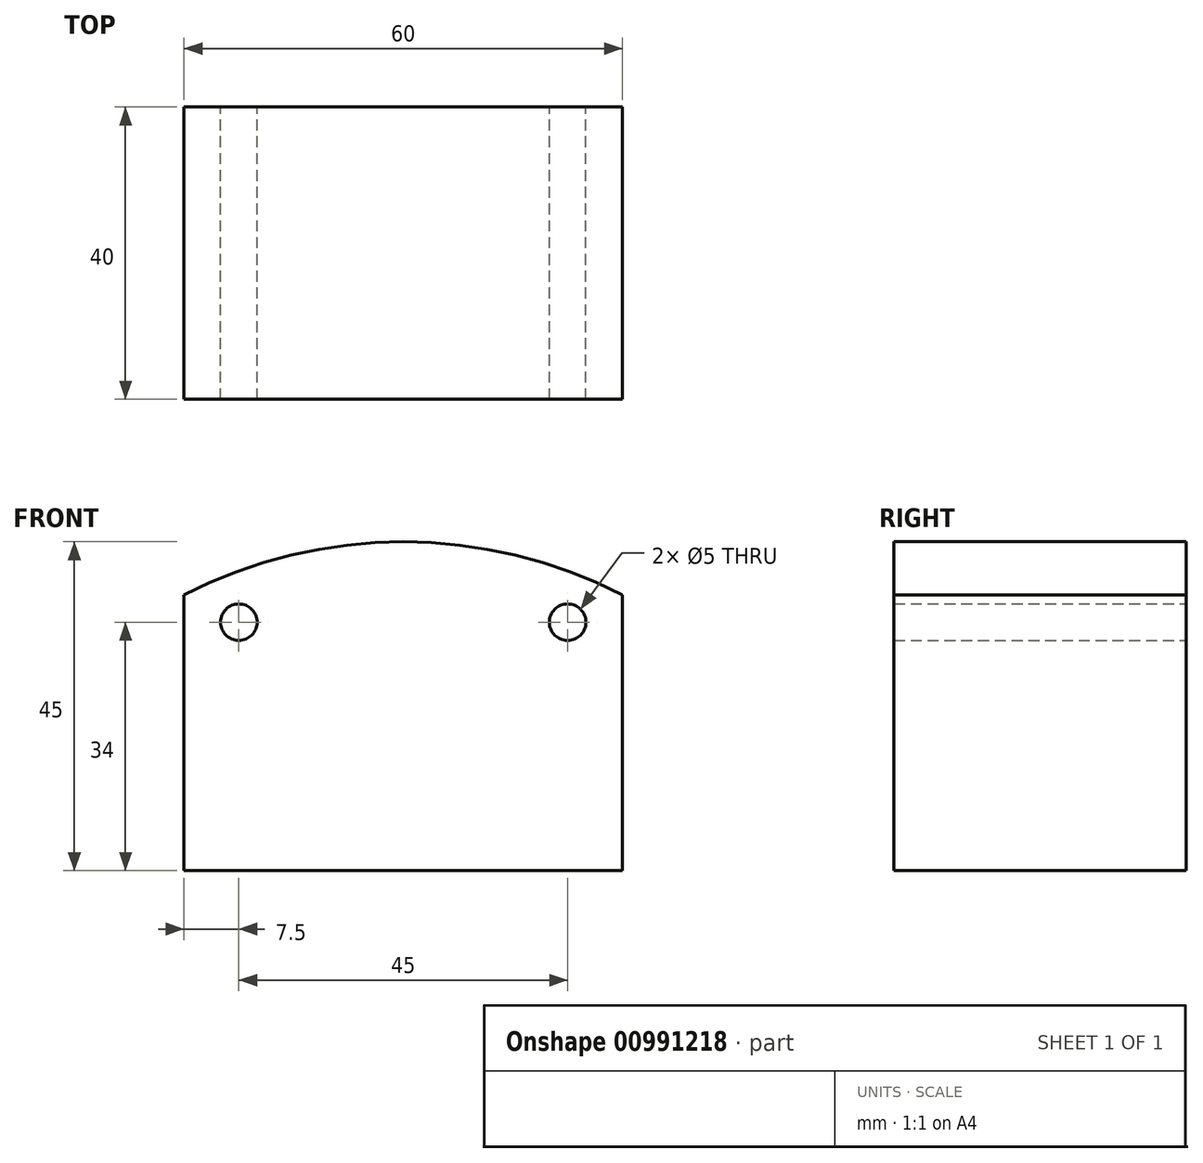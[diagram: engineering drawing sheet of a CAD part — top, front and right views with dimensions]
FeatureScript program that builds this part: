
annotation { "Feature Type Name" : "Feature", "Feature Type Description" : "" }
export const myFeature = defineFeature(function(context is Context, id is Id, definition is map)
    precondition{}
    {
        {
            var Q0;
            Q0=qCreatedBy(makeId("Front.planeOp"),FACE);
            var sketch = newSketch(context, id + "F0", { "sketchPlane" : qUnion([Q0])});
            skLineSegment(sketch, "E0.bottom", {"start": v(0, 0) * mm, "end": v(60, 0) * mm});
            skLineSegment(sketch, "E0.left", {"start": v(0, 0) * mm, "end": v(0, 37.7) * mm});
            skLineSegment(sketch, "E0.right", {"start": v(60, 0) * mm, "end": v(60, 37.7) * mm});
            skPoint(sketch, "E1", {"position": v(7.5, 34) * mm});
            skPoint(sketch, "E2", {"position": v(52.5, 34) * mm});
            skPoint(sketch, "E3", {"position": v(30, 0) * mm});
            skPoint(sketch, "E4", {"position": v(30, -20.33) * mm});
            skArc(sketch, "E5", {"start": v(60, 37.7) * mm, "mid": v(30, 45) * mm, "end": v(0, 37.7) * mm});
            skCircle(sketch, "E6", {"center": v(7.5, 34) * mm, "radius": 2.5 * mm});
            skCircle(sketch, "E7", {"center": v(52.5, 34) * mm, "radius": 2.5 * mm});
            skSolve(sketch);
        }
        {
            var Q0;
            Q0=makeQuery(id+"F0.imprint","IMPRINT",FACE,{"disambiguationData":[TD([[makeQuery(id+"F0.imprint","IMPRINT",EDGE,{"derivedFrom":sQuery(id+"F0.wireOp",EDGE,"E0.bottom")}),1.0]])]});
            extrude(context, id + "F1", {"entities" : qUnion([Q0]), "depth" : 40 * mm, "offsetDistance" : 25 * mm});
        }
    });
